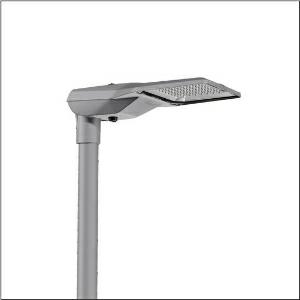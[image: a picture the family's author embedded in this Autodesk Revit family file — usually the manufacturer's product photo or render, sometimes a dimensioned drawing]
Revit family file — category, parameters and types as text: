
# Revit family: streetlight_sl_21_midi___st1_0a_5xe3d23t08nb_7d41
name_source: partatom
category: Lighting Fixtures
units: mm (PartAtom-declared; Revit-internal decimal feet)

## family parameters
Cut with Voids When Loaded = No
Host = Face
Light Source = No
Part Type = Normal
Room Calculation Point = No
Round Connector Dimension = Use Diameter
Shared = No

## types (1)
- --- (1 x LED, 18780 lm, 151.2 W, 2200K)
    Apparent Load = 151 VA
    CIE Flux Codes = 40 73 97 100 100
    Color Rendering = 70
    Color Temperature = 2200K
    Default Elevation = 1800 mm
    Description = Streetlight SL 21 midi, mast luminaire, primary light control with lens, of PMMA, primary optical cover: cover, of toughened safety glass, transparent, light distribution: ST1.0a, light emission: direct distribution, primary light characteristic: asymmetric, installation type: side-entry, post-top, LED, High Power LED, rated luminous flux: 18.780lm, luminous efficacy: 124lm/W, light colour: 722, colour temperature: 2200K, control gear: D4i, control: overheat protection, constant luminous flux control, time-dependent luminous flux control, flexible luminous flux parameterisation, pre-setting: logarithmic dimming characteristic, mains connection: 230..240V, AC, 50/60Hz, start of lifetime: 151W, end of service life: 157W, reduction: 70W, luminaire housing, of diecast aluminium, powder-coated, SITECO metallic grey (DB 702S), corrosivity category C5 high according to DIN EN ISO 12944, please order mast flange separately, inclination adjustable: 0°, 5°, 10°, 15°, sealing non-destructively replaceable, multi-level sealing system, length: 644mm, width: 335mm, height: 110mm, mast flange for spigot size: 42mm (side-entry): 5XC10008XM4, 60/48mm (side-entry/post-top): 5XC10108XM2, 76/60mm (side-entry/post-top): 5XC10108XM1, mounting height: 4..8m, Smart Interface below and above, protection rating (complete): IP66, insulation class (complete): insulation class II (safety insulation), certification: CE, ENEC, ENEC+, VDE, impact resistance: IK10, permissible operating ambient temperature for outdoor applications: -40..+50°C, standard-compliant lighting for roads and squares, packaging unit: 1 piece

Light Distribution: ST1.0a
    Height = 111 mm
    Lamp = 1 x LED
    Lamp Light Flux = 18780 lm
    Lamp Power = 151.2 W
    Lamp count = 1
    Length = 644 mm
    Luminous efficacy = 124 lm/W
    Manufacturer = Siteco
    ModVariant = No
    Model = 5XE3D23T08NB
    Number of Poles = 1
    OnlyDefault = Yes
    Power Factor = 1
    Product Name = Streetlight SL 21 midi | ST1.0a
    Product group = mast luminaire | pylon top
    ProductGroupID = 6100
    Protection Class = Protection class II
    Protection Degree = IP 66
    RLX_Detail_Level = 1
    RLX_Emergency_Light_Flux = 0 lm
    RLX_Emergency_Type = 0
    RLX_Emergency_Type_DB = No
    RlxData = <blob elided: 27081 chars, md5=2f9debd8>
    Socket = socket
    Standby Power = 0 W
    System Light Flux = 18781 lm
    System Power = 151 W
    Type Comments = factory setting: luminous flux: 100 % | dim-lin: 254 | 802 mA
    Type Image = l_1004304.jpg
    URL = http://relux.com
    VarID = @adj_170015
    Voltage = 0 V
    Weight = 0.00 kg
    Width = 336 mm

## geometry (parser evidence)
native form markers: Blend x4, Sweep x12
no freeform markers — native parametric forms only
